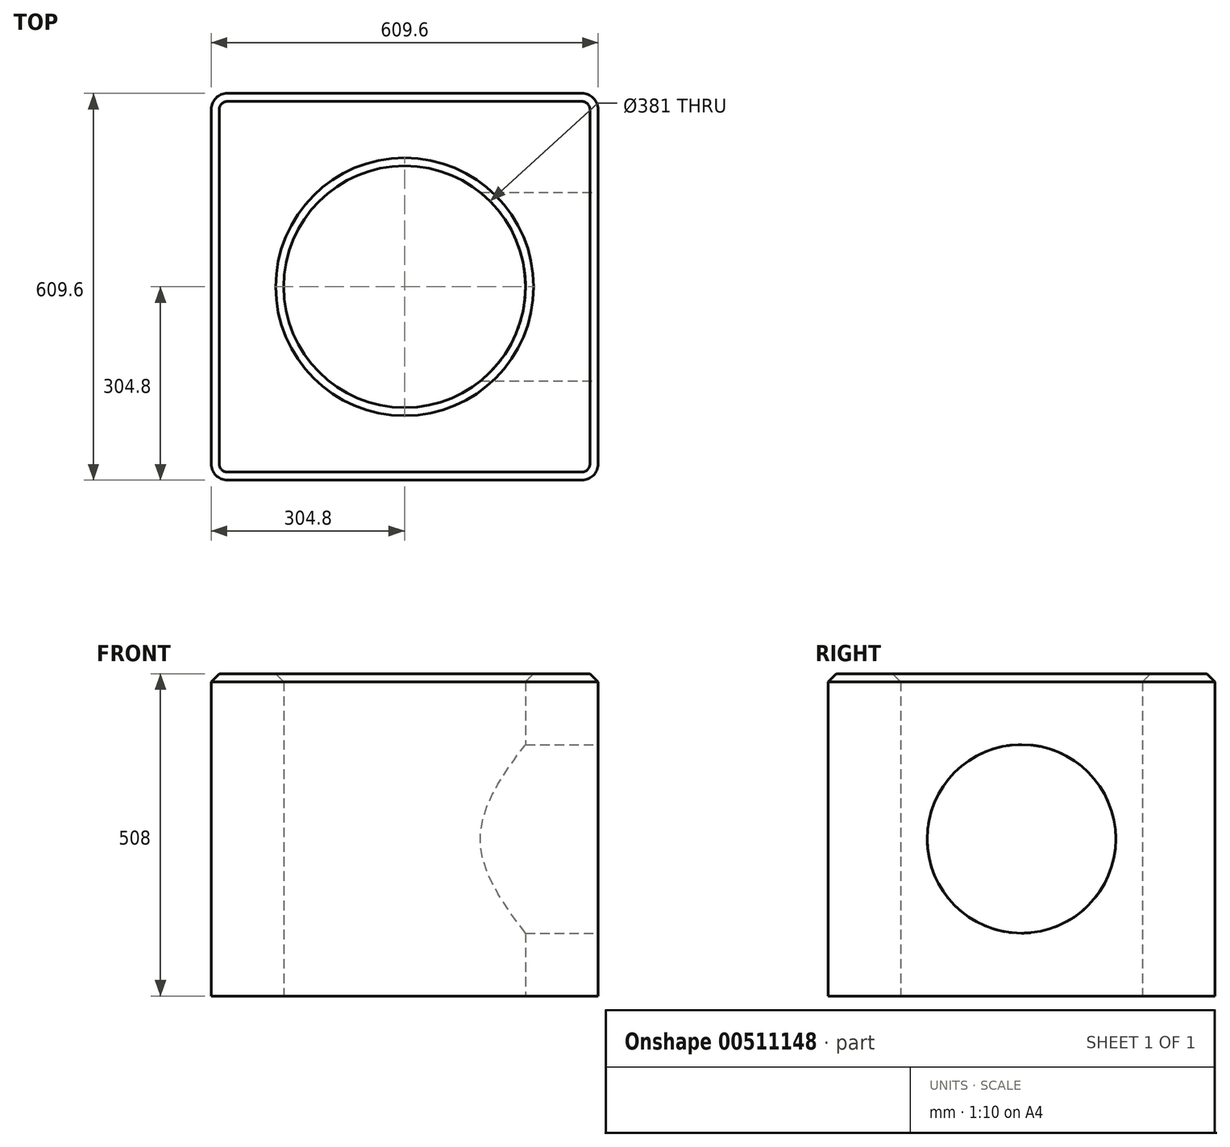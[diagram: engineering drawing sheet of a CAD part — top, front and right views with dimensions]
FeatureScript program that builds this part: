
annotation { "Feature Type Name" : "Feature", "Feature Type Description" : "" }
export const myFeature = defineFeature(function(context is Context, id is Id, definition is map)
    precondition{}
    {
        {
            var Q0;
            Q0=qCreatedBy(makeId("Top.planeOp"),FACE);
            var sketch = newSketch(context, id + "F0", { "sketchPlane" : qUnion([Q0])});
            skLineSegment(sketch, "E0.bottom", {"start": v(-279.4, 304.8) * mm, "end": v(279.4, 304.8) * mm});
            skLineSegment(sketch, "E0.top", {"start": v(-279.4, -304.8) * mm, "end": v(279.4, -304.8) * mm});
            skLineSegment(sketch, "E0.left", {"start": v(-304.8, 279.4) * mm, "end": v(-304.8, -279.4) * mm});
            skLineSegment(sketch, "E0.right", {"start": v(304.8, 279.4) * mm, "end": v(304.8, -279.4) * mm});
            skPoint(sketch, "E0.middle", {"position": v(0, 0) * mm});
            skPoint(sketch, "E1.visualSharp", {"position": v(-304.8, -304.8) * mm});
            skArc(sketch, "E1.filletArc", {"start": v(-304.8, -279.4) * mm, "mid": v(-297.36, -297.36) * mm, "end": v(-279.4, -304.8) * mm});
            skPoint(sketch, "E2.visualSharp", {"position": v(-304.8, 304.8) * mm});
            skArc(sketch, "E2.filletArc", {"start": v(-279.4, 304.8) * mm, "mid": v(-297.36, 297.36) * mm, "end": v(-304.8, 279.4) * mm});
            skPoint(sketch, "E3.visualSharp", {"position": v(304.8, 304.8) * mm});
            skArc(sketch, "E3.filletArc", {"start": v(304.8, 279.4) * mm, "mid": v(297.36, 297.36) * mm, "end": v(279.4, 304.8) * mm});
            skPoint(sketch, "E4.visualSharp", {"position": v(304.8, -304.8) * mm});
            skArc(sketch, "E4.filletArc", {"start": v(279.4, -304.8) * mm, "mid": v(297.36, -297.36) * mm, "end": v(304.8, -279.4) * mm});
            skCircle(sketch, "E5", {"center": v(0, 0) * mm, "radius": 190.5 * mm});
            skLineSegment(sketch, "E6", {"start": v(-190.5, 0) * mm, "end": v(-304.8, 0) * mm});
            skPoint(sketch, "E6.startSnap0", {"position": v(-304.8, 0) * mm});
            skLineSegment(sketch, "E7", {"start": v(-304.8, 0) * mm, "end": v(190.5, 0) * mm});
            skLineSegment(sketch, "E8", {"start": v(190.5, 0) * mm, "end": v(304.8, 0) * mm});
            skLineSegment(sketch, "E9", {"start": v(0, -304.8) * mm, "end": v(0, -190.5) * mm});
            skLineSegment(sketch, "E10", {"start": v(0, 304.8) * mm, "end": v(0, 190.5) * mm});
            skPoint(sketch, "E10.endSnap0", {"position": v(0, 304.8) * mm});
            skSolve(sketch);
        }
        {
            var Q0;
            {var subQ4=sQuery(id+"F0.wireOp",EDGE,"E1.filletArc");Q0=makeQuery(id+"F0.imprint","IMPRINT",FACE,{"disambiguationData":[TD([[makeQuery(id+"F0.imprint","IMPRINT",EDGE,{"derivedFrom":subQ4}),1.0]])]});}
            var Q1;
            {var subQ3=sQuery(id+"F0.wireOp",EDGE,"E4.filletArc");Q1=makeQuery(id+"F0.imprint","IMPRINT",FACE,{"disambiguationData":[TD([[makeQuery(id+"F0.imprint","IMPRINT",EDGE,{"derivedFrom":subQ3}),1.0]])]});}
            var Q2;
            {var subQ3=sQuery(id+"F0.wireOp",EDGE,"E3.filletArc");Q2=makeQuery(id+"F0.imprint","IMPRINT",FACE,{"disambiguationData":[TD([[makeQuery(id+"F0.imprint","IMPRINT",EDGE,{"derivedFrom":subQ3}),1.0]])]});}
            var Q3;
            {var subQ4=sQuery(id+"F0.wireOp",EDGE,"E2.filletArc");Q3=makeQuery(id+"F0.imprint","IMPRINT",FACE,{"disambiguationData":[TD([[makeQuery(id+"F0.imprint","IMPRINT",EDGE,{"derivedFrom":subQ4}),1.0]])]});}
            extrude(context, id + "F1", {"entities" : qUnion([Q0, Q1, Q2, Q3]), "depth" : 508 * mm});
        }
        {
            var Q0;
            Q0=makeQuery(id+"F1.opExtrude","CAP_EDGE",EDGE,{"disambiguationData":[OSD([sQuery(id+"F0.wireOp",EDGE,"E0.bottom")])],"isStart":false});
            var Q1;
            Q1=makeQuery(id+"F1.opExtrude","CAP_EDGE",EDGE,{"disambiguationData":[OSD([sQuery(id+"F0.wireOp",EDGE,"E5")])],"isStart":false});
            chamfer(context, id + "F2", {"entities" : qUnion([Q0, Q1]), "width" : 12.7 * mm, "tangentPropagation" : true});
        }
        {
            var Q0;
            Q0=makeQuery(id+"F1.opExtrude","SWEPT_FACE",FACE,{"disambiguationData":[OSD([sQuery(id+"F0.wireOp",EDGE,"E0.right")])]});
            var sketch = newSketch(context, id + "F3", { "sketchPlane" : qUnion([Q0])});
            skCircle(sketch, "E11", {"center": v(0, 247.65) * mm, "radius": 148.6 * mm});
            skPoint(sketch, "E11.centerSnap0", {"position": v(-279.4, 247.65) * mm});
            skSolve(sketch);
        }
        {
            var Q0;
            Q0 = qSketchRegion(id + "F3", true);
            extrude(context, id + "F4", {"entities" : qUnion([Q0]), "operationType" : NewBodyOperationType.REMOVE, "oppositeDirection" : true, "depth" : 189.61 * mm, "hasSecondDirection" : true, "secondDirectionOppositeDirection" : false, "secondDirectionDepth" : 166.1 * mm});
        }
    });
